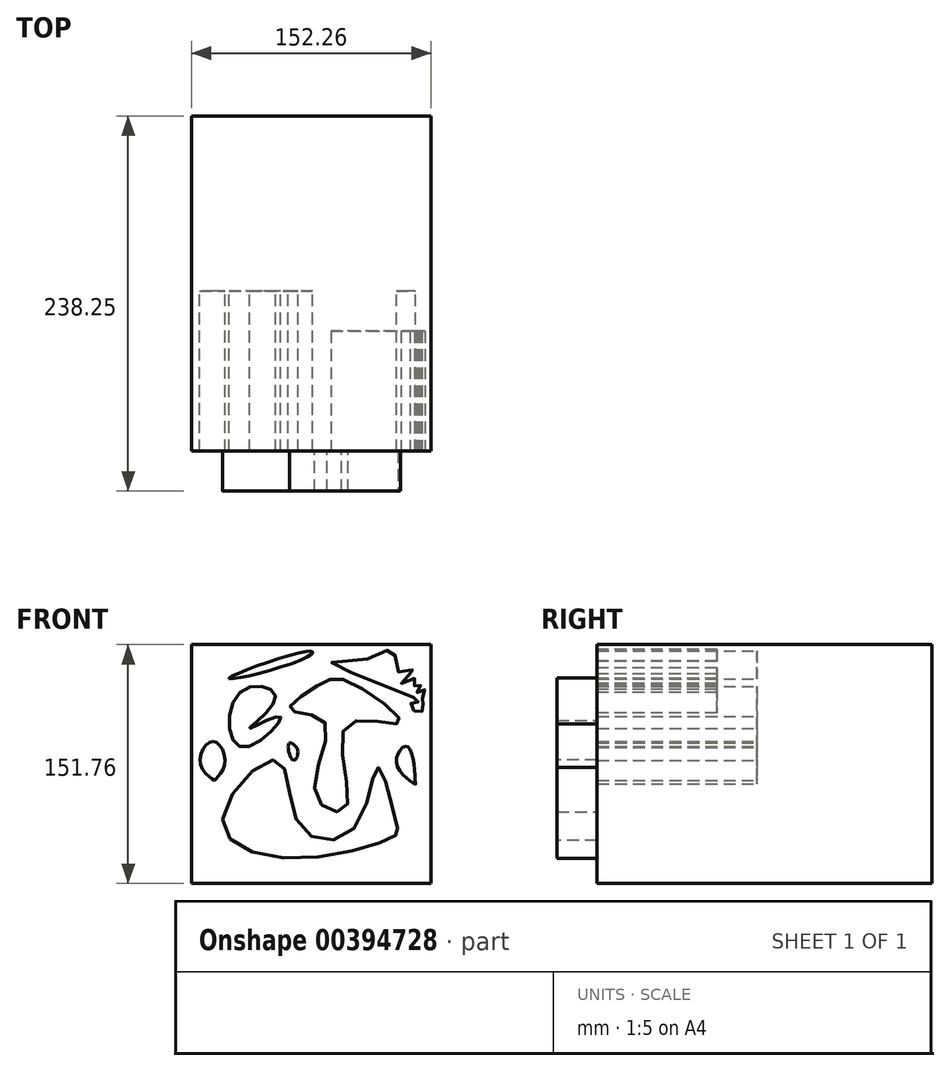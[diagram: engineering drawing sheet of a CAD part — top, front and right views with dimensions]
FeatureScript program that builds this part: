
annotation { "Feature Type Name" : "Feature", "Feature Type Description" : "" }
export const myFeature = defineFeature(function(context is Context, id is Id, definition is map)
    precondition{}
    {
        {
            var Q0;
            Q0=qCreatedBy(makeId("Front.planeOp"),FACE);
            var sketch = newSketch(context, id + "F0", { "sketchPlane" : qUnion([Q0])});
            skLineSegment(sketch, "E0.bottom", {"start": v(-76.13, 75.88) * mm, "end": v(76.13, 75.88) * mm});
            skLineSegment(sketch, "E0.top", {"start": v(-76.13, -75.88) * mm, "end": v(76.13, -75.88) * mm});
            skLineSegment(sketch, "E0.left", {"start": v(-76.13, 75.88) * mm, "end": v(-76.13, -75.88) * mm});
            skLineSegment(sketch, "E0.right", {"start": v(76.13, 75.88) * mm, "end": v(76.13, -75.88) * mm});
            skPoint(sketch, "E0.middle", {"position": v(0, 0) * mm});
            skSolve(sketch);
        }
        {
            var Q0;
            Q0 = qSketchRegion(id + "F0", true);
            extrude(context, id + "F1", {"entities" : qUnion([Q0]), "depth" : 85.85 * mm});
        }
        {
            var Q0;
            Q0=makeQuery(id+"F1.opExtrude","CAP_FACE",FACE,{"disambiguationData":[OSD([sQuery(id+"F0.wireOp",EDGE,"E0.bottom"),sQuery(id+"F0.wireOp",EDGE,"E0.top"),sQuery(id+"F0.wireOp",EDGE,"E0.left"),sQuery(id+"F0.wireOp",EDGE,"E0.right")])],"isStart":false});
            var sketch = newSketch(context, id + "F2", { "sketchPlane" : qUnion([Q0])});
            skFitSpline(sketch, "E1", {"points": [v(-45.18, 45.48) * mm, v(-44.17, 10.74) * mm, v(-19.68, 30.02) * mm, v(-39.15, 22.59) * mm, v(-22.69, 42.26) * mm, v(-45.18, 45.48) * mm]});
            skFitSpline(sketch, "E2", {"points": [v(3.81, 49.5) * mm, v(-13.45, 34.63) * mm, v(8.43, 27) * mm, v(3.01, -20.38) * mm, v(21.88, -27.8) * mm, v(22.49, 24.8) * mm, v(56.42, 26.2) * mm, v(23.09, 52.9) * mm, v(3.81, 49.5) * mm]});
            skFitSpline(sketch, "E3", {"points": [v(-56.22, -35.04) * mm, v(-11.04, -59.93) * mm, v(53.8, -45.28) * mm, v(54.61, -39.45) * mm, v(42.56, -2.1) * mm, v(27.5, -40.46) * mm, v(-7.23, -39.25) * mm, v(-21.68, 2.3) * mm, v(-56.22, -35.04) * mm]});
            skFitSpline(sketch, "E4", {"points": [v(-14.05, 12.95) * mm, v(-11.44, 2.5) * mm, v(-8.63, 8.93) * mm, v(-14.05, 12.95) * mm]});
            skFitSpline(sketch, "E5", {"points": [v(-62.24, 14.36) * mm, v(-70.47, 0) * mm, v(-61.24, -10.34) * mm, v(-61.04, -10.14) * mm, v(-55.01, 0) * mm, v(-62.24, 14.36) * mm]});
            skFitSpline(sketch, "E6", {"points": [v(61.44, 10.94) * mm, v(54.21, 0) * mm, v(66.26, -12.75) * mm, v(66.26, -12.55) * mm, v(61.44, 10.94) * mm]});
            skFitSpline(sketch, "E7", {"points": [v(0, 71.78) * mm, v(-2.61, 67.96) * mm, v(-52.2, 54.51) * mm, v(0, 71.78) * mm]});
            skFitSpline(sketch, "E8", {"points": [v(65.05, 42.26) * mm, v(12.85, 64.55) * mm, v(34.13, 66.36) * mm, v(52.4, 71.98) * mm, v(56.82, 57.52) * mm, v(66.26, 60.94) * mm, v(57.22, 51.3) * mm, v(66.86, 54.31) * mm, v(65.65, 49.1) * mm, v(69.47, 49.9) * mm, v(66.86, 45.48) * mm, v(72.08, 47.48) * mm, v(69.87, 43.27) * mm, v(72.28, 39.65) * mm, v(70.27, 36.84) * mm, v(70.27, 33.23) * mm, v(66.46, 33.03) * mm, v(62.84, 38.05) * mm, v(66.26, 38.65) * mm, v(68.26, 40.06) * mm, v(65.05, 42.26) * mm]});
            skSolve(sketch);
        }
        {
            var Q0;
            Q0 = qSketchRegion(id + "F2", true);
            extrude(context, id + "F3", {"entities" : qUnion([Q0]), "operationType" : NewBodyOperationType.ADD, "depth" : 25.4 * mm});
        }
        {
            var Q0;
            Q0=makeQuery(id+"F1.opExtrude","CAP_FACE",FACE,{"disambiguationData":[OSD([sQuery(id+"F0.wireOp",EDGE,"E0.bottom"),sQuery(id+"F0.wireOp",EDGE,"E0.top"),sQuery(id+"F0.wireOp",EDGE,"E0.left"),sQuery(id+"F0.wireOp",EDGE,"E0.right")])],"isStart":false});
            var Q1;
            Q1=makeQuery(id+"F3.opExtrude","CAP_FACE",FACE,{"disambiguationData":[OSD([sQuery(id+"F2.wireOp",EDGE,"E3")])],"isStart":false});
            extrude(context, id + "F4", {"entities" : qUnion([Q0, Q1]), "operationType" : NewBodyOperationType.ADD, "depth" : 127 * mm});
        }
        {
            var Q0;
            Q0=makeQuery(id+"F3.opExtrude","CAP_FACE",FACE,{"disambiguationData":[OSD([sQuery(id+"F2.wireOp",EDGE,"E2")])],"isStart":false});
            extrude(context, id + "F5", {"entities" : qUnion([Q0]), "operationType" : NewBodyOperationType.ADD, "depth" : 127 * mm});
        }
        {
            var Q0;
            Q0=makeQuery(id+"F3.opExtrude","CAP_FACE",FACE,{"disambiguationData":[OSD([sQuery(id+"F2.wireOp",EDGE,"E8")])],"isStart":false});
            extrude(context, id + "F6", {"entities" : qUnion([Q0]), "operationType" : NewBodyOperationType.ADD, "depth" : 25.4 * mm});
        }
    });
